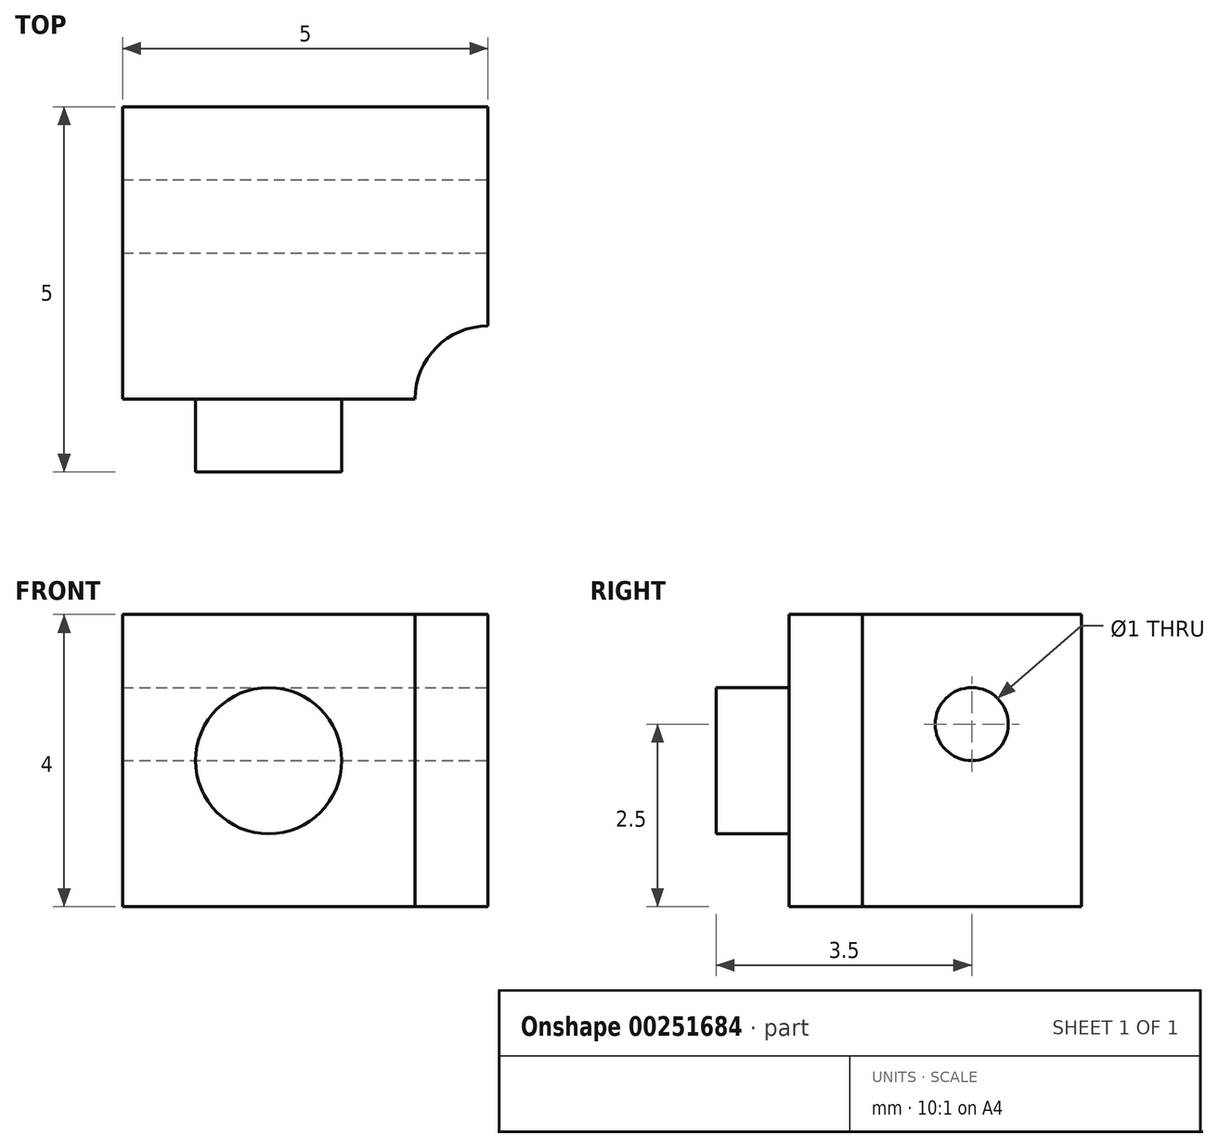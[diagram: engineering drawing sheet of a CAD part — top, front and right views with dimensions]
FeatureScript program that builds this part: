
annotation { "Feature Type Name" : "Feature", "Feature Type Description" : "" }
export const myFeature = defineFeature(function(context is Context, id is Id, definition is map)
    precondition{}
    {
        {
            var Q0;
            Q0=qCreatedBy(makeId("Top.planeOp"),FACE);
            var sketch = newSketch(context, id + "F0", { "sketchPlane" : qUnion([Q0])});
            skLineSegment(sketch, "E0.bottom", {"start": v(0, 0) * mm, "end": v(5, 0) * mm});
            skLineSegment(sketch, "E0.top", {"start": v(0, 4) * mm, "end": v(5, 4) * mm});
            skLineSegment(sketch, "E0.left", {"start": v(0, 0) * mm, "end": v(0, 4) * mm});
            skLineSegment(sketch, "E0.right", {"start": v(5, 0) * mm, "end": v(5, 4) * mm});
            skSolve(sketch);
        }
        {
            var Q0;
            Q0 = qSketchRegion(id + "F0", true);
            extrude(context, id + "F1", {"entities" : qUnion([Q0]), "depth" : 4 * mm});
        }
        {
            var Q0;
            Q0=makeQuery(id+"F1.opExtrude","CAP_FACE",FACE,{"disambiguationData":[OSD([sQuery(id+"F0.wireOp",EDGE,"E0.bottom"),sQuery(id+"F0.wireOp",EDGE,"E0.top"),sQuery(id+"F0.wireOp",EDGE,"E0.left"),sQuery(id+"F0.wireOp",EDGE,"E0.right")])],"isStart":false});
            var sketch = newSketch(context, id + "F2", { "sketchPlane" : qUnion([Q0])});
            skArc(sketch, "E1", {"start": v(5, 1) * mm, "mid": v(4.3, 0.7) * mm, "end": v(4, 0) * mm});
            skLineSegment(sketch, "E2", {"start": v(5, 0) * mm, "end": v(5, 1) * mm, "construction": true});
            skLineSegment(sketch, "E3", {"start": v(5, 0) * mm, "end": v(4, 0) * mm, "construction": true});
            skSolve(sketch);
        }
        {
            var Q0;
            {var subQ0=sQuery(id+"F2.wireOp",EDGE,"E1");Q0=makeQuery(id+"F2.imprint","IMPRINT",FACE,{"disambiguationData":[TD([[makeQuery(id+"F2.imprint","IMPRINT",EDGE,{"derivedFrom":subQ0}),1.0]])]});}
            extrude(context, id + "F3", {"entities" : qUnion([Q0]), "operationType" : NewBodyOperationType.REMOVE, "oppositeDirection" : true, "depth" : 25 * mm});
        }
        {
            var Q0;
            Q0=makeQuery(id+"F1.opExtrude","SWEPT_FACE",FACE,{"disambiguationData":[OSD([sQuery(id+"F0.wireOp",EDGE,"E0.bottom")])]});
            var sketch = newSketch(context, id + "F4", { "sketchPlane" : qUnion([Q0])});
            skLineSegment(sketch, "E4", {"start": v(0, 2) * mm, "end": v(2, 2) * mm, "construction": true});
            skCircle(sketch, "E5", {"center": v(2, 2) * mm, "radius": 1 * mm});
            skSolve(sketch);
        }
        {
            var Q0;
            Q0 = qSketchRegion(id + "F4", true);
            extrude(context, id + "F5", {"entities" : qUnion([Q0]), "operationType" : NewBodyOperationType.ADD, "depth" : 1 * mm});
        }
        {
            var Q0;
            Q0=makeQuery(id+"F1.opExtrude","SWEPT_FACE",FACE,{"disambiguationData":[OSD([sQuery(id+"F0.wireOp",EDGE,"E0.right")])]});
            var sketch = newSketch(context, id + "F6", { "sketchPlane" : qUnion([Q0])});
            skLineSegment(sketch, "E6", {"start": v(2.5, 4) * mm, "end": v(2.5, 2.5) * mm, "construction": true});
            skCircle(sketch, "E7", {"center": v(2.5, 2.5) * mm, "radius": 0.5 * mm});
            skSolve(sketch);
        }
        {
            var Q0;
            Q0 = qSketchRegion(id + "F6", true);
            extrude(context, id + "F7", {"entities" : qUnion([Q0]), "operationType" : NewBodyOperationType.REMOVE, "oppositeDirection" : true, "depth" : 25 * mm});
        }
    });
